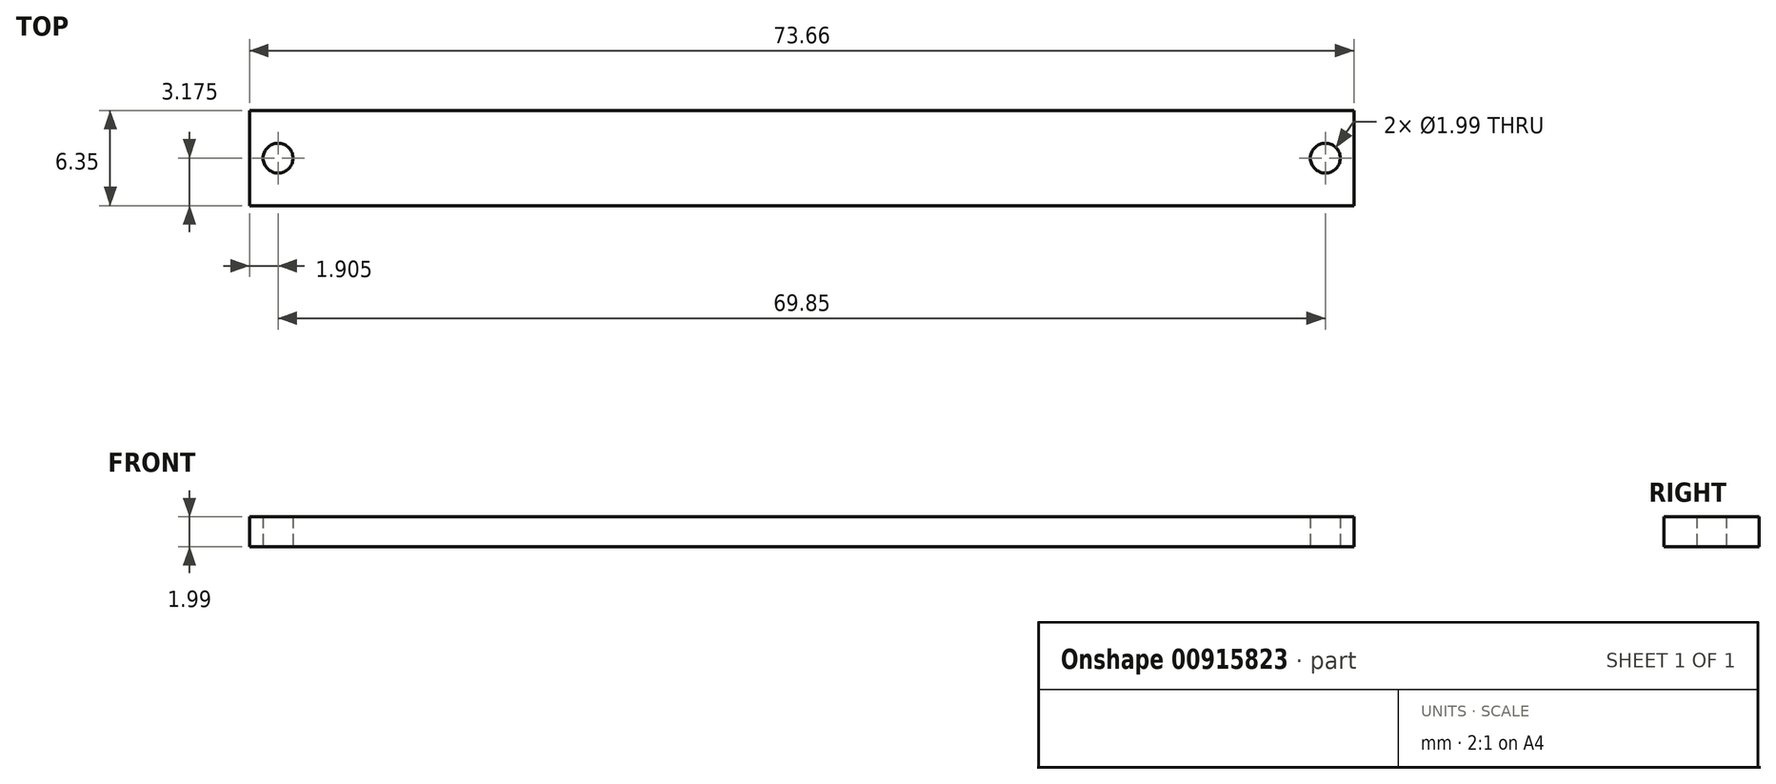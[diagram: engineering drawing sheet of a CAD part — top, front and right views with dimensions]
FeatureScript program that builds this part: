
annotation { "Feature Type Name" : "Feature", "Feature Type Description" : "" }
export const myFeature = defineFeature(function(context is Context, id is Id, definition is map)
    precondition{}
    {
        {
            var Q0;
            Q0=qCreatedBy(makeId("Top.planeOp"),FACE);
            var sketch = newSketch(context, id + "F0", { "sketchPlane" : qUnion([Q0])});
            skLineSegment(sketch, "E0.bottom", {"start": v(0, 0) * mm, "end": v(73.66, 0) * mm});
            skLineSegment(sketch, "E0.top", {"start": v(0, -6.35) * mm, "end": v(73.66, -6.35) * mm});
            skLineSegment(sketch, "E0.left", {"start": v(0, 0) * mm, "end": v(0, -6.35) * mm});
            skLineSegment(sketch, "E0.right", {"start": v(73.66, 0) * mm, "end": v(73.66, -6.35) * mm});
            skCircle(sketch, "E1", {"center": v(1.9, -3.17) * mm, "radius": 1 * mm});
            skPoint(sketch, "E1.centerSnap0", {"position": v(0, -3.17) * mm});
            skLineSegment(sketch, "E2", {"start": v(36.83, 0) * mm, "end": v(36.83, -2.02) * mm, "construction": true});
            skCircle(sketch, "E3.MirrorC", {"center": v(71.76, -3.17) * mm, "radius": 1 * mm});
            skSolve(sketch);
        }
        {
            var Q0;
            Q0=makeQuery(id+"F0.imprint","IMPRINT",FACE,{"disambiguationData":[TD([[makeQuery(id+"F0.imprint","IMPRINT",EDGE,{"derivedFrom":sQuery(id+"F0.wireOp",EDGE,"E0.bottom")}),-1.0]])]});
            extrude(context, id + "F1", {"entities" : qUnion([Q0]), "depth" : 2 * mm, "offsetDistance" : 25.4 * mm});
        }
    });
